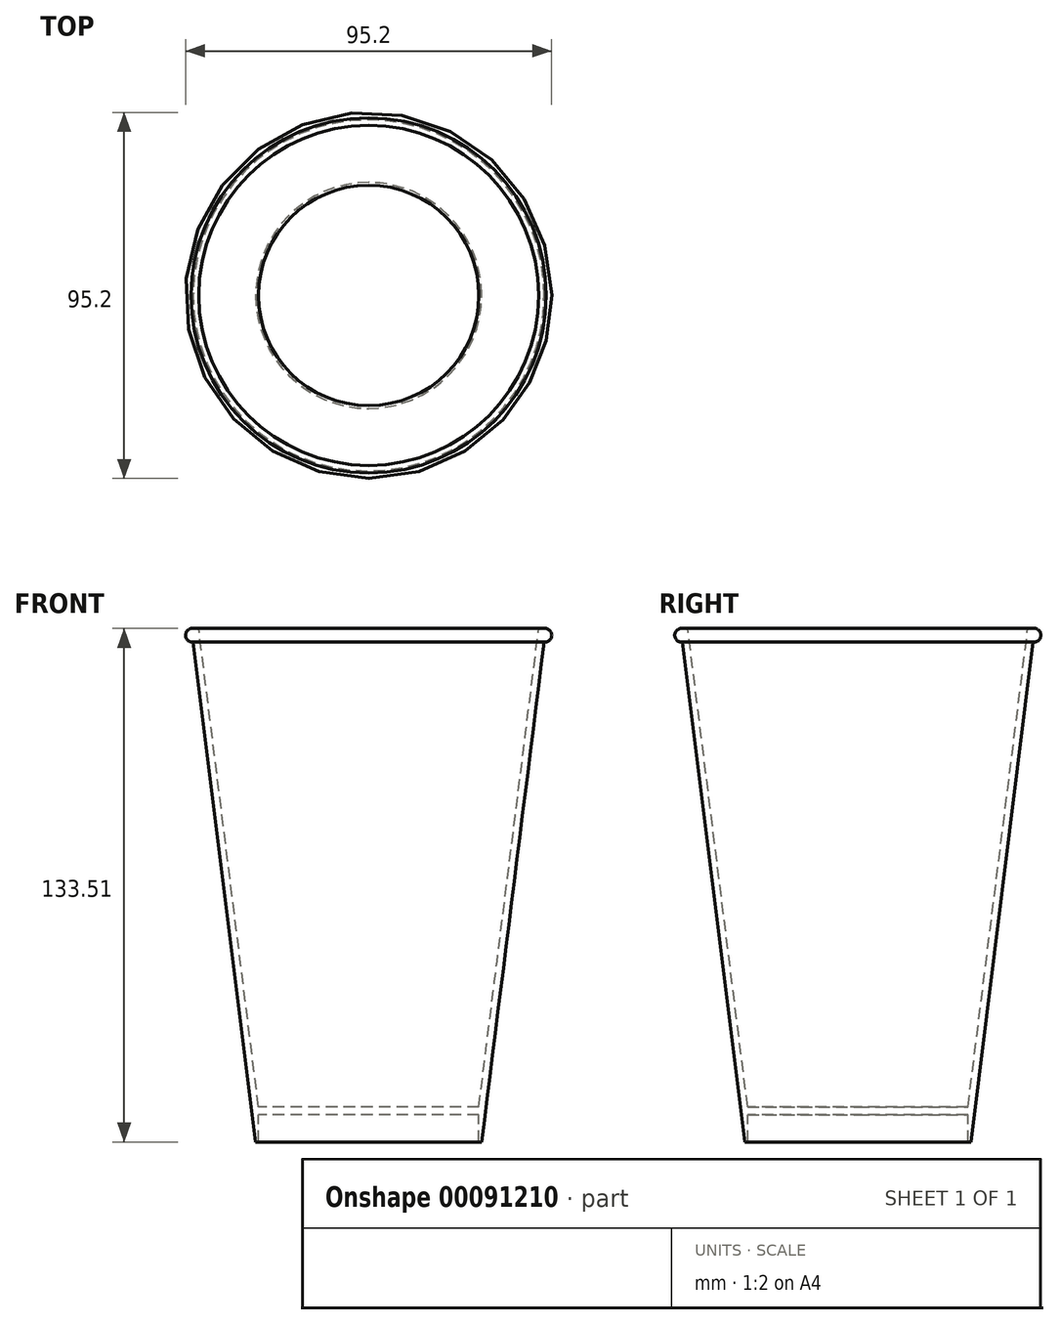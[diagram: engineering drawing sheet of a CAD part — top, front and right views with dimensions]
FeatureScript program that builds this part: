
annotation { "Feature Type Name" : "Feature", "Feature Type Description" : "" }
export const myFeature = defineFeature(function(context is Context, id is Id, definition is map)
    precondition{}
    {
        {
            var Q0;
            Q0=qCreatedBy(makeId("Front.planeOp"),FACE);
            var sketch = newSketch(context, id + "F0", { "sketchPlane" : qUnion([Q0])});
            skLineSegment(sketch, "E0", {"start": v(0, 62.55) * mm, "end": v(0, -70.75) * mm});
            skLineSegment(sketch, "E1", {"start": v(0, -70.75) * mm, "end": v(29.4, -70.75) * mm});
            skLineSegment(sketch, "E2", {"start": v(29.4, -70.75) * mm, "end": v(46.12, 62.55) * mm});
            skLineSegment(sketch, "E3", {"start": v(46.12, 62.55) * mm, "end": v(0, 62.55) * mm});
            skArc(sketch, "E4", {"start": v(46.12, 62.55) * mm, "mid": v(47.99, 60.43) * mm, "end": v(45.66, 58.85) * mm});
            skSolve(sketch);
        }
        {
            var Q0;
            Q0=qCreatedBy(makeId("Top.planeOp"),FACE);
            cPlane(context, id + "F1", {"entities" : qUnion([Q0]), "cplaneType" : CPlaneType.OFFSET, "offset" : 62 * mm, "oppositeDirection" : true, "width" : 150 * mm, "height" : 150 * mm});
        }
        {
            var Q0;
            Q0=qCreatedBy(makeId("Front.planeOp"),FACE);
            var sketch = newSketch(context, id + "F2", { "sketchPlane" : qUnion([Q0])});
            skLineSegment(sketch, "E5", {"start": v(44.2, 62.76) * mm, "end": v(28.66, -61.64) * mm});
            skLineSegment(sketch, "E6", {"start": v(28.66, -61.64) * mm, "end": v(0, -61.64) * mm});
            skLineSegment(sketch, "E7", {"start": v(0, -61.64) * mm, "end": v(0, -63.64) * mm});
            skLineSegment(sketch, "E8", {"start": v(0, -63.64) * mm, "end": v(28.66, -63.64) * mm});
            skLineSegment(sketch, "E9", {"start": v(28.66, -63.64) * mm, "end": v(28.66, -70.75) * mm});
            skLineSegment(sketch, "E10", {"start": v(28.66, -70.75) * mm, "end": v(29.38, -70.75) * mm});
            skLineSegment(sketch, "E11", {"start": v(29.38, -70.75) * mm, "end": v(45.62, 59.2) * mm});
            skLineSegment(sketch, "E12", {"start": v(44.2, 62.76) * mm, "end": v(46.18, 62.76) * mm});
            skArc(sketch, "E13", {"start": v(45.62, 59.2) * mm, "mid": v(47.58, 60.72) * mm, "end": v(46.18, 62.76) * mm});
            skSolve(sketch);
        }
        {
            var Q0;
            Q0 = qSketchRegion(id + "F2", true);
            var Q1;
            Q1=sQuery(id+"F0.wireOp",EDGE,"E0");
            revolve(context, id + "F3", {"entities" : qUnion([Q0]), "axis" : qUnion([Q1]), "revolveType" : RevolveType.FULL});
        }
    });
